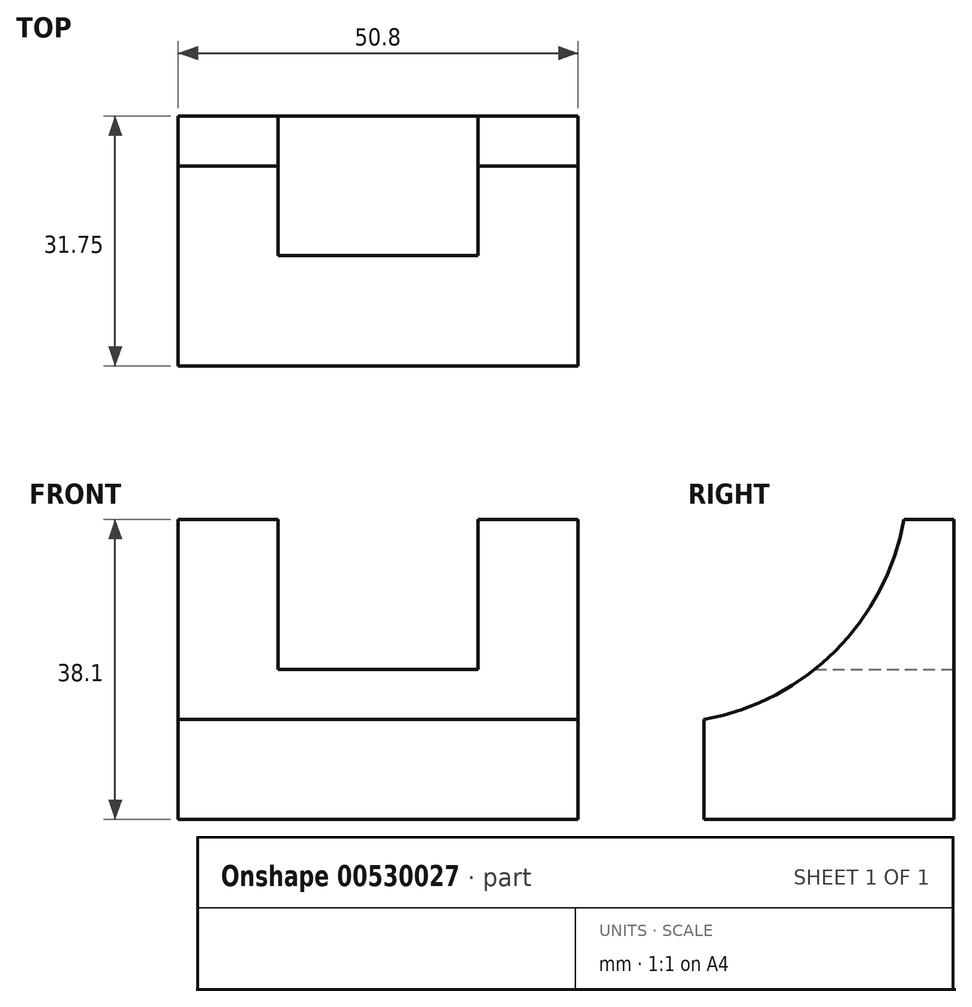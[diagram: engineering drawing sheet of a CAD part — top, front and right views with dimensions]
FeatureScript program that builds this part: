
annotation { "Feature Type Name" : "Feature", "Feature Type Description" : "" }
export const myFeature = defineFeature(function(context is Context, id is Id, definition is map)
    precondition{}
    {
        {
            var Q0;
            Q0=qCreatedBy(makeId("Right.planeOp"),FACE);
            var sketch = newSketch(context, id + "F0", { "sketchPlane" : qUnion([Q0])});
            skLineSegment(sketch, "E0", {"start": v(-15.3, 52.38) * mm, "end": v(-15.3, 14.28) * mm});
            skLineSegment(sketch, "E1", {"start": v(-15.3, 14.28) * mm, "end": v(-47.06, 14.28) * mm});
            skLineSegment(sketch, "E2", {"start": v(-47.06, 14.28) * mm, "end": v(-47.06, 26.98) * mm});
            skLineSegment(sketch, "E3", {"start": v(-15.3, 52.38) * mm, "end": v(-21.66, 52.38) * mm});
            skArc(sketch, "E4", {"start": v(-47.06, 26.98) * mm, "mid": v(-30.37, 35.7) * mm, "end": v(-21.66, 52.38) * mm});
            skSolve(sketch);
        }
        {
            var Q0;
            Q0=makeQuery(id+"F0.imprint","IMPRINT",FACE,{"disambiguationData":[TD([[makeQuery(id+"F0.imprint","IMPRINT",EDGE,{"derivedFrom":sQuery(id+"F0.wireOp",EDGE,"E0")}),-1.0]])]});
            extrude(context, id + "F1", {"entities" : qUnion([Q0]), "depth" : 50.8 * mm, "offsetDistance" : 25.4 * mm});
        }
        {
            var Q0;
            Q0=makeQuery(id+"F1.opExtrude","SWEPT_FACE",FACE,{"disambiguationData":[OSD([sQuery(id+"F0.wireOp",EDGE,"E0")])]});
            var sketch = newSketch(context, id + "F2", { "sketchPlane" : qUnion([Q0])});
            skLineSegment(sketch, "E5", {"start": v(-38.1, 52.38) * mm, "end": v(-38.1, 33.33) * mm});
            skLineSegment(sketch, "E6", {"start": v(-38.1, 33.33) * mm, "end": v(-12.7, 33.33) * mm});
            skLineSegment(sketch, "E7", {"start": v(-12.7, 33.33) * mm, "end": v(-12.7, 52.38) * mm});
            skLineSegment(sketch, "E8", {"start": v(-38.1, 52.38) * mm, "end": v(-12.7, 52.38) * mm});
            skLineSegment(sketch, "E9", {"start": v(-50.8, 52.38) * mm, "end": v(-38.1, 52.38) * mm});
            skLineSegment(sketch, "E10", {"start": v(-12.7, 52.38) * mm, "end": v(0, 52.38) * mm});
            skSolve(sketch);
        }
        {
            var Q0;
            Q0=makeQuery(id+"F2.imprint","IMPRINT",FACE,{"disambiguationData":[TD([[makeQuery(id+"F2.imprint","IMPRINT",EDGE,{"derivedFrom":sQuery(id+"F2.wireOp",EDGE,"E5")}),1.0]])]});
            extrude(context, id + "F3", {"entities" : qUnion([Q0]), "operationType" : NewBodyOperationType.REMOVE, "endBound" : BoundingType.THROUGH_ALL, "oppositeDirection" : true, "depth" : 25.4 * mm, "offsetDistance" : 25.4 * mm});
        }
    });
